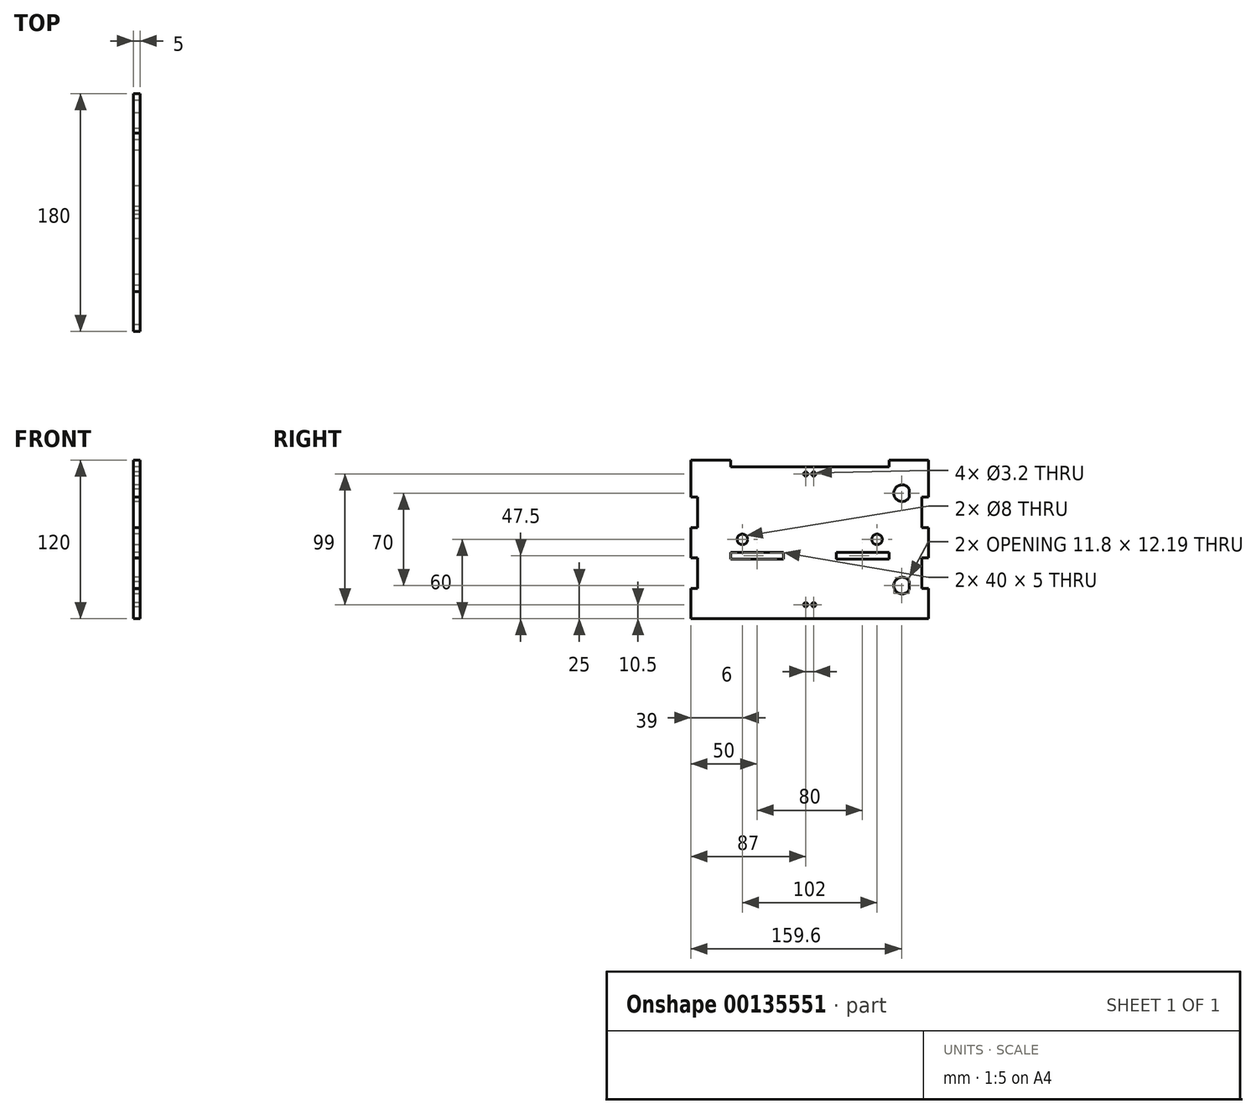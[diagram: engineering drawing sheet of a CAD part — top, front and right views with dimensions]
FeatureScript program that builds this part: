
annotation { "Feature Type Name" : "Feature", "Feature Type Description" : "" }
export const myFeature = defineFeature(function(context is Context, id is Id, definition is map)
    precondition{}
    {
        {
            var Q0;
            Q0=qCreatedBy(makeId("Right.planeOp"),FACE);
            var sketch = newSketch(context, id + "F0", { "sketchPlane" : qUnion([Q0])});
            skPoint(sketch, "E0.end.orphan", {"position": v(0, -15) * mm});
            skLineSegment(sketch, "E1", {"start": v(100, 0) * mm, "end": v(-100, 0) * mm, "construction": true});
            skLineSegment(sketch, "E2", {"start": v(0, 75) * mm, "end": v(0, -75) * mm, "construction": true});
            skLineSegment(sketch, "E3.bottom", {"start": v(90, 60) * mm, "end": v(60, 60) * mm});
            skLineSegment(sketch, "E3.top", {"start": v(90, -60) * mm, "end": v(-90, -60) * mm});
            skLineSegment(sketch, "E3.left", {"start": v(90, 60) * mm, "end": v(90, 32) * mm});
            skLineSegment(sketch, "E3.right", {"start": v(-90, 60) * mm, "end": v(-90, 31.36) * mm});
            skLineSegment(sketch, "E4", {"start": v(83.18, -10) * mm, "end": v(-83.18, -10) * mm, "construction": true});
            skLineSegment(sketch, "E5.bottom", {"start": v(85, 55) * mm, "end": v(-85, 55) * mm, "construction": true});
            skLineSegment(sketch, "E5.top", {"start": v(85, -55) * mm, "end": v(-85, -55) * mm, "construction": true});
            skLineSegment(sketch, "E5.left", {"start": v(85, 55) * mm, "end": v(85, -55) * mm, "construction": true});
            skLineSegment(sketch, "E5.right", {"start": v(-85, 55) * mm, "end": v(-85, -55) * mm, "construction": true});
            skLineSegment(sketch, "E6", {"start": v(-83.25, -15) * mm, "end": v(83.25, -15) * mm, "construction": true});
            skPoint(sketch, "E7", {"position": v(0, 0) * mm});
            skLineSegment(sketch, "E8", {"start": v(92.57, 10) * mm, "end": v(-115.44, 10) * mm, "construction": true});
            skLineSegment(sketch, "E9", {"start": v(60, 60) * mm, "end": v(60, 55) * mm});
            skLineSegment(sketch, "E10", {"start": v(-60, 60) * mm, "end": v(-60, 55) * mm});
            skLineSegment(sketch, "E11", {"start": v(60, 55) * mm, "end": v(-60, 55) * mm});
            skLineSegment(sketch, "E12", {"start": v(-90, -37) * mm, "end": v(-85, -37) * mm});
            skLineSegment(sketch, "E13.direction1", {"start": v(-90, -37) * mm, "end": v(-125, -37) * mm, "construction": true});
            skLineSegment(sketch, "E14", {"start": v(-85, -37) * mm, "end": v(-85, -14) * mm});
            skLineSegment(sketch, "E15", {"start": v(-85, 8.36) * mm, "end": v(-85, 31.36) * mm});
            skLineSegment(sketch, "E16.trimOffspring", {"start": v(-90, -37) * mm, "end": v(-90, -60) * mm});
            skLineSegment(sketch, "E17.trimOffspring", {"start": v(-90, 8.36) * mm, "end": v(-90, -14.64) * mm});
            skLineSegment(sketch, "E18.0.1.0", {"start": v(-90, -14) * mm, "end": v(-85, -14) * mm});
            skLineSegment(sketch, "E18.0.2.0", {"start": v(-90, 9) * mm, "end": v(-85, 9) * mm});
            skLineSegment(sketch, "E18.0.3.0", {"start": v(-90, 32) * mm, "end": v(-85, 32) * mm});
            skLineSegment(sketch, "E18.direction2", {"start": v(-90, -37) * mm, "end": v(-90, -14.64) * mm, "construction": true});
            skLineSegment(sketch, "E19", {"start": v(90, -37) * mm, "end": v(85, -37) * mm});
            skLineSegment(sketch, "E20.trimOffspring", {"start": v(90, -37) * mm, "end": v(90, -60) * mm});
            skLineSegment(sketch, "E21", {"start": v(85, -37) * mm, "end": v(85, -24.11) * mm});
            skLineSegment(sketch, "E22.0.1.0", {"start": v(90, -14) * mm, "end": v(85, -14) * mm});
            skLineSegment(sketch, "E22.0.2.0", {"start": v(90, 9) * mm, "end": v(85, 9) * mm});
            skLineSegment(sketch, "E22.0.3.0", {"start": v(90, 32) * mm, "end": v(85, 32) * mm});
            skLineSegment(sketch, "E22.direction1", {"start": v(85, -37) * mm, "end": v(100, -37) * mm, "construction": true});
            skLineSegment(sketch, "E22.direction2", {"start": v(85, -37) * mm, "end": v(85, -14) * mm, "construction": true});
            skLineSegment(sketch, "E23", {"start": v(85, 32) * mm, "end": v(85, 9) * mm});
            skLineSegment(sketch, "E24", {"start": v(85, -24.11) * mm, "end": v(85, -14) * mm});
            skLineSegment(sketch, "E25.trimOffspring", {"start": v(90, 9) * mm, "end": v(90, -14) * mm});
            skLineSegment(sketch, "E26.trimOffspring", {"start": v(-60, 60) * mm, "end": v(-90, 60) * mm});
            skLineSegment(sketch, "E27", {"start": v(85, 49.5) * mm, "end": v(-85, 49.5) * mm, "construction": true});
            skCircle(sketch, "E28", {"center": v(3, 49.5) * mm, "radius": 1.6 * mm});
            skCircle(sketch, "E29", {"center": v(-3, 49.5) * mm, "radius": 1.6 * mm});
            skLineSegment(sketch, "E30.bottom", {"start": v(60, -10) * mm, "end": v(20, -10) * mm});
            skLineSegment(sketch, "E30.top", {"start": v(60, -15) * mm, "end": v(20, -15) * mm});
            skLineSegment(sketch, "E30.left", {"start": v(60, -10) * mm, "end": v(60, -15) * mm});
            skLineSegment(sketch, "E30.right", {"start": v(20, -10) * mm, "end": v(20, -15) * mm});
            skLineSegment(sketch, "E31.bottom", {"start": v(-20, -10) * mm, "end": v(-60, -10) * mm});
            skLineSegment(sketch, "E31.top", {"start": v(-20, -15) * mm, "end": v(-60, -15) * mm});
            skLineSegment(sketch, "E31.left", {"start": v(-20, -10) * mm, "end": v(-20, -15) * mm});
            skLineSegment(sketch, "E31.right", {"start": v(-60, -10) * mm, "end": v(-60, -15) * mm});
            skLineSegment(sketch, "E32", {"start": v(85, -49.5) * mm, "end": v(-85, -49.5) * mm, "construction": true});
            skCircle(sketch, "E33", {"center": v(3, -49.5) * mm, "radius": 1.6 * mm});
            skCircle(sketch, "E34.MirrorC", {"center": v(-3, -49.5) * mm, "radius": 1.6 * mm});
            skLineSegment(sketch, "E35.trimOffspring", {"start": v(0.05, -10) * mm, "end": v(0.05, -9.26) * mm, "construction": true});
            skLineSegment(sketch, "E36", {"start": v(-85, -14) * mm, "end": v(-85, -37) * mm});
            skLineSegment(sketch, "E37", {"start": v(-85, 32) * mm, "end": v(-85, 9) * mm});
            skLineSegment(sketch, "E38", {"start": v(-90, 8.36) * mm, "end": v(-90, 9) * mm});
            skSolve(sketch);
        }
        {
            var Q0;
            Q0=makeQuery(id+"F0.imprint","IMPRINT",FACE,{"disambiguationData":[TD([[makeQuery(id+"F0.imprint","IMPRINT",EDGE,{"derivedFrom":sQuery(id+"F0.wireOp",EDGE,"E3.bottom")}),1.0]])]});
            var sketch = newSketch(context, id + "F1", { "sketchPlane" : qUnion([Q0])});
            skLineSegment(sketch, "E39", {"start": v(-51, 0) * mm, "end": v(51, 0) * mm, "construction": true});
            skCircle(sketch, "E40", {"center": v(-51, 0) * mm, "radius": 4 * mm});
            skCircle(sketch, "E41", {"center": v(51, 0) * mm, "radius": 4 * mm});
            skLineSegment(sketch, "E42", {"start": v(51, 0) * mm, "end": v(51, 21.8) * mm, "construction": true});
            skLineSegment(sketch, "E43", {"start": v(51, 0) * mm, "end": v(63.78, 0) * mm, "construction": true});
            skSolve(sketch);
        }
        {
            var Q0;
            Q0=makeQuery(id+"F0.imprint","IMPRINT",FACE,{"disambiguationData":[TD([[makeQuery(id+"F0.imprint","IMPRINT",EDGE,{"derivedFrom":sQuery(id+"F0.wireOp",EDGE,"E3.bottom")}),1.0]])]});
            var sketch = newSketch(context, id + "F2", { "sketchPlane" : qUnion([Q0])});
            skCircle(sketch, "E44", {"center": v(70, 35) * mm, "radius": 8.75 * mm, "construction": true});
            skArc(sketch, "E45", {"start": v(75.5, 38.07) * mm, "mid": v(63.7, 35) * mm, "end": v(75.5, 31.93) * mm});
            skLineSegment(sketch, "E46", {"start": v(75.5, 38.07) * mm, "end": v(75.5, 31.93) * mm});
            skLineSegment(sketch, "E47", {"start": v(70, 35) * mm, "end": v(70, 43.75) * mm, "construction": true});
            skLineSegment(sketch, "E48", {"start": v(70, 35) * mm, "end": v(61.25, 35) * mm, "construction": true});
            skSolve(sketch);
        }
        {
            var Q0;
            Q0=makeQuery(id+"F0.imprint","IMPRINT",FACE,{"disambiguationData":[TD([[makeQuery(id+"F0.imprint","IMPRINT",EDGE,{"derivedFrom":sQuery(id+"F0.wireOp",EDGE,"E3.bottom")}),1.0]])]});
            var sketch = newSketch(context, id + "F3", { "sketchPlane" : qUnion([Q0])});
            skCircle(sketch, "E49", {"center": v(70, -35) * mm, "radius": 8.75 * mm, "construction": true});
            skArc(sketch, "E50", {"start": v(75.5, -31.93) * mm, "mid": v(63.7, -35) * mm, "end": v(75.5, -38.07) * mm});
            skLineSegment(sketch, "E51", {"start": v(75.5, -31.93) * mm, "end": v(75.5, -38.07) * mm});
            skLineSegment(sketch, "E52", {"start": v(70, -35) * mm, "end": v(70, -26.25) * mm, "construction": true});
            skLineSegment(sketch, "E53", {"start": v(70, -35) * mm, "end": v(61.25, -35) * mm, "construction": true});
            skSolve(sketch);
        }
        {
            var Q0;
            Q0 = qSketchRegion(id + "F0", true);
            extrude(context, id + "F4", {"entities" : qUnion([Q0]), "depth" : 5 * mm});
        }
        {
            var Q0;
            Q0 = qSketchRegion(id + "F1", true);
            var Q1;
            Q1 = qSketchRegion(id + "F2", true);
            var Q2;
            Q2 = qSketchRegion(id + "F3", true);
            extrude(context, id + "F5", {"entities" : qUnion([Q0, Q1, Q2]), "operationType" : NewBodyOperationType.REMOVE, "depth" : 5 * mm});
        }
    });
